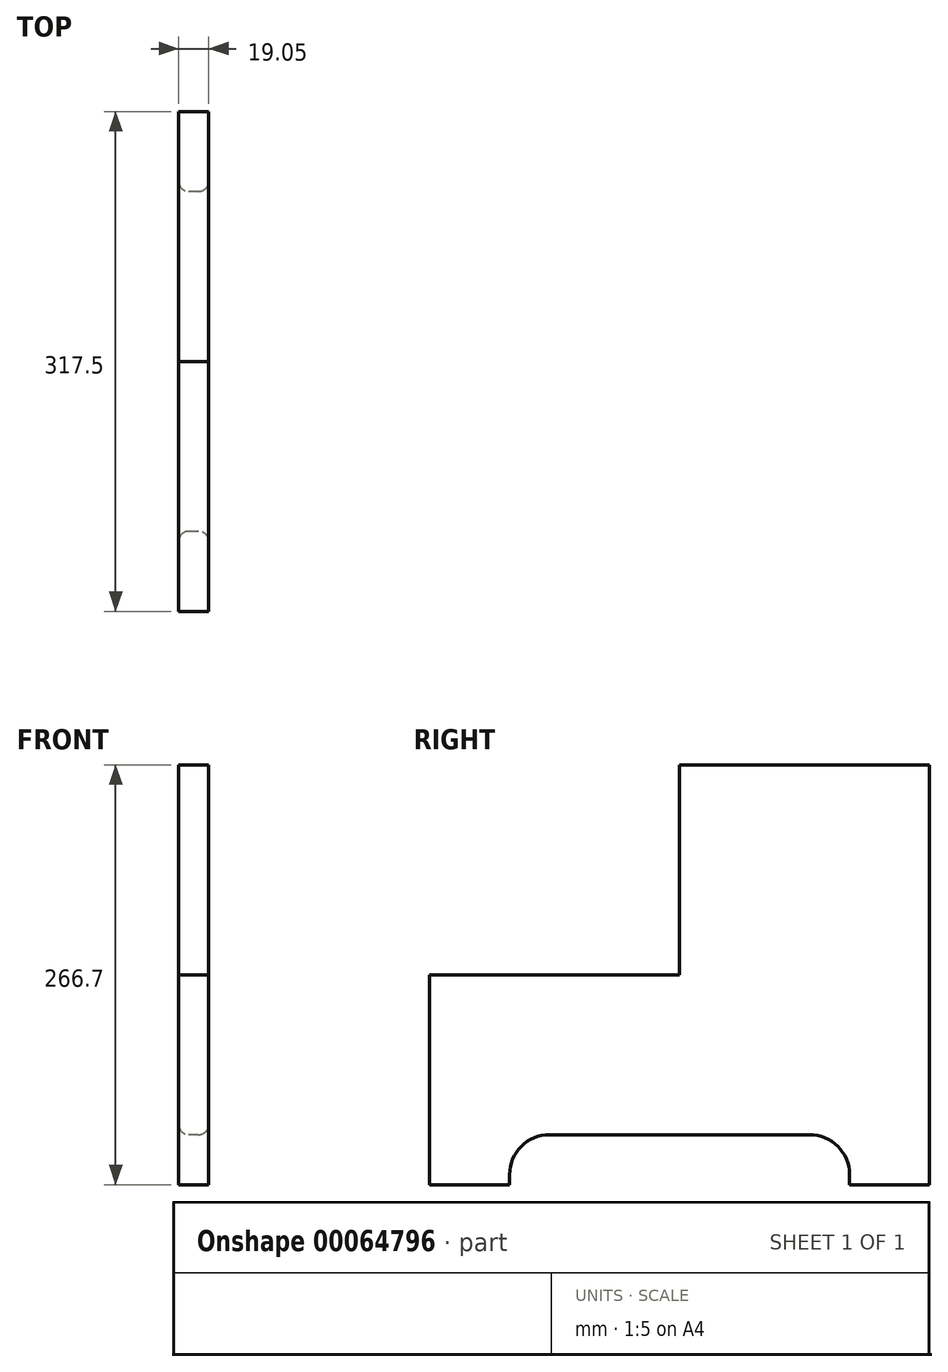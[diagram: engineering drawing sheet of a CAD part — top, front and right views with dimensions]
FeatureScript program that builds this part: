
annotation { "Feature Type Name" : "Feature", "Feature Type Description" : "" }
export const myFeature = defineFeature(function(context is Context, id is Id, definition is map)
    precondition{}
    {
        {
            var Q0;
            Q0=qCreatedBy(makeId("Right.planeOp"),FACE);
            var sketch = newSketch(context, id + "F0", { "sketchPlane" : qUnion([Q0])});
            skLineSegment(sketch, "E0", {"start": v(0, 0) * mm, "end": v(0, 133.35) * mm});
            skLineSegment(sketch, "E1", {"start": v(0, 133.35) * mm, "end": v(158.75, 133.35) * mm});
            skLineSegment(sketch, "E2", {"start": v(158.75, 133.35) * mm, "end": v(158.75, 266.7) * mm});
            skLineSegment(sketch, "E3", {"start": v(158.75, 266.7) * mm, "end": v(317.5, 266.7) * mm});
            skLineSegment(sketch, "E4", {"start": v(317.5, 266.7) * mm, "end": v(317.5, 0) * mm});
            skLineSegment(sketch, "E5", {"start": v(317.5, 0) * mm, "end": v(266.7, 0) * mm});
            skLineSegment(sketch, "E6", {"start": v(50.8, 0) * mm, "end": v(50.8, 6.35) * mm});
            skLineSegment(sketch, "E7", {"start": v(76.2, 31.75) * mm, "end": v(241.3, 31.75) * mm});
            skLineSegment(sketch, "E8", {"start": v(266.7, 6.35) * mm, "end": v(266.7, 0) * mm});
            skPoint(sketch, "E9.visualSharp", {"position": v(50.8, 31.75) * mm});
            skArc(sketch, "E9.filletArc", {"start": v(76.2, 31.75) * mm, "mid": v(58.24, 24.31) * mm, "end": v(50.8, 6.35) * mm});
            skPoint(sketch, "E10.visualSharp", {"position": v(266.7, 31.75) * mm});
            skArc(sketch, "E10.filletArc", {"start": v(266.7, 6.35) * mm, "mid": v(259.26, 24.31) * mm, "end": v(241.3, 31.75) * mm});
            skLineSegment(sketch, "E11.trimOffspring", {"start": v(50.8, 0) * mm, "end": v(0, 0) * mm});
            skSolve(sketch);
        }
        {
            var Q0;
            Q0=makeQuery(id+"F0.imprint","IMPRINT",FACE,{"disambiguationData":[TD([[makeQuery(id+"F0.imprint","IMPRINT",EDGE,{"derivedFrom":sQuery(id+"F0.wireOp",EDGE,"E0")}),-1.0]])]});
            extrude(context, id + "F1", {"entities" : qUnion([Q0]), "depth" : 19.05 * mm});
        }
        {
            var Q0;
            Q0=makeQuery(id+"F1.opExtrude","CAP_EDGE",EDGE,{"disambiguationData":[OSD([sQuery(id+"F0.wireOp",EDGE,"E7")])],"isStart":false});
            fillet(context, id + "F2", {"entities" : qUnion([Q0]), "radius" : 6.35 * mm, "tangentPropagation" : true, "allowEdgeOverflow" : false});
        }
        {
            var Q0;
            Q0=makeQuery(id+"F1.opExtrude","CAP_EDGE",EDGE,{"disambiguationData":[OSD([sQuery(id+"F0.wireOp",EDGE,"E7")])],"isStart":true});
            fillet(context, id + "F3", {"entities" : qUnion([Q0]), "radius" : 6.35 * mm, "tangentPropagation" : true, "allowEdgeOverflow" : false});
        }
    });
